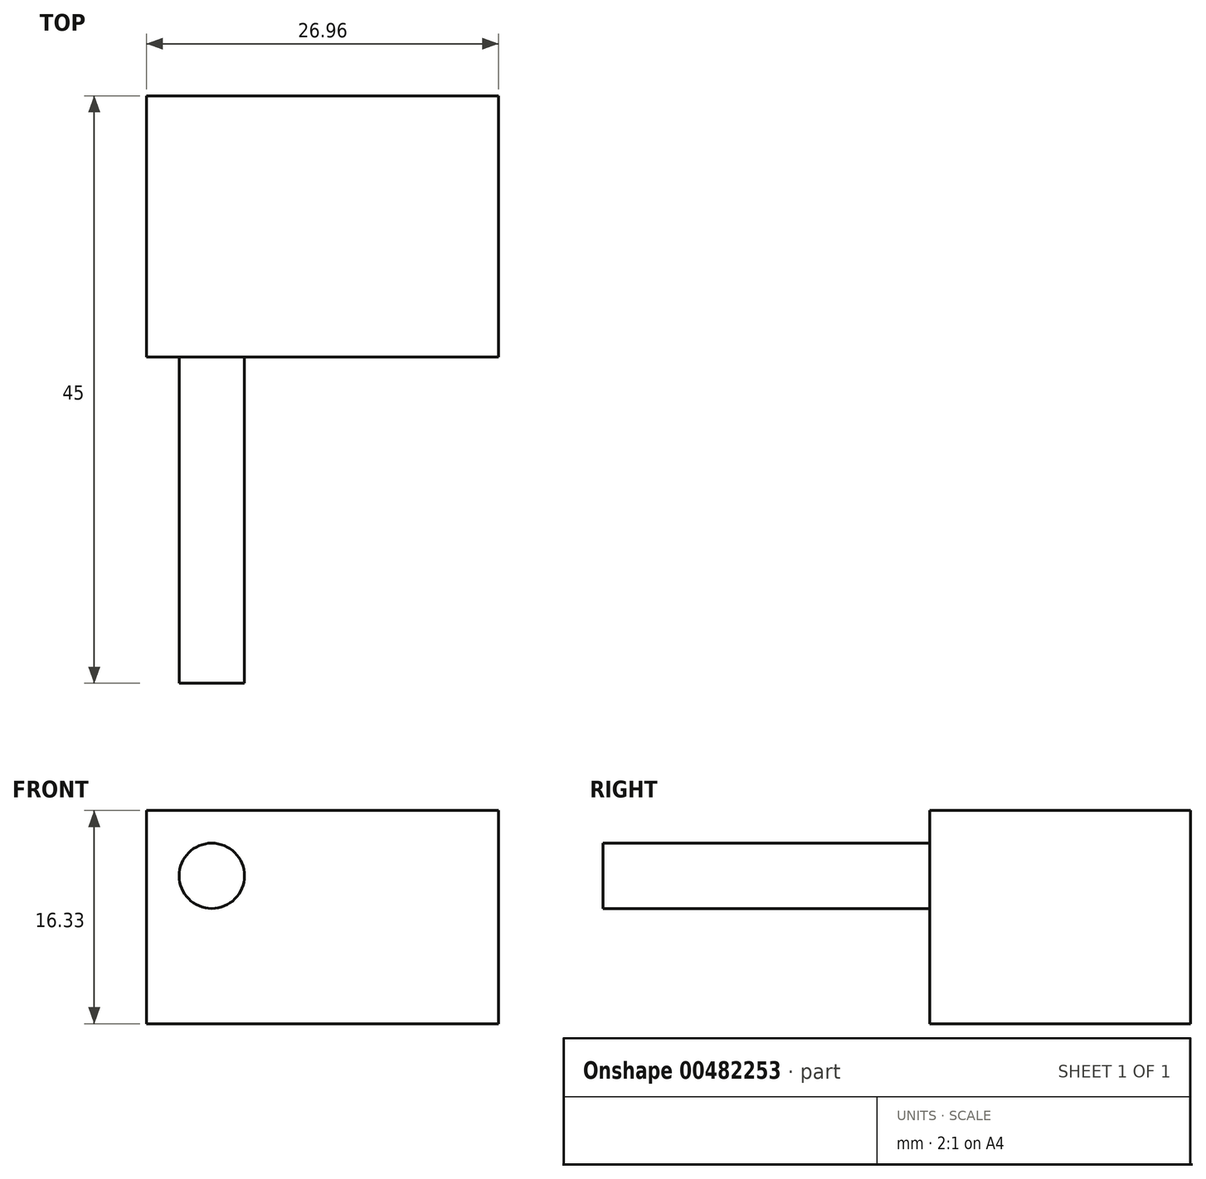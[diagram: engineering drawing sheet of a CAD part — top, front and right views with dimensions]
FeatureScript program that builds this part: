
annotation { "Feature Type Name" : "Feature", "Feature Type Description" : "" }
export const myFeature = defineFeature(function(context is Context, id is Id, definition is map)
    precondition{}
    {
        {
            var Q0;
            Q0=qCreatedBy(makeId("Front.planeOp"),FACE);
            var sketch = newSketch(context, id + "F0", { "sketchPlane" : qUnion([Q0])});
            skLineSegment(sketch, "E0.bottom", {"start": v(-68.77, 60.6) * mm, "end": v(-41.8, 60.6) * mm});
            skLineSegment(sketch, "E0.top", {"start": v(-68.77, 44.28) * mm, "end": v(-41.8, 44.28) * mm});
            skLineSegment(sketch, "E0.left", {"start": v(-68.77, 60.6) * mm, "end": v(-68.77, 44.28) * mm});
            skLineSegment(sketch, "E0.right", {"start": v(-41.8, 60.6) * mm, "end": v(-41.8, 44.28) * mm});
            skSolve(sketch);
        }
        {
            var Q0;
            Q0=makeQuery(id+"F0.imprint","IMPRINT",FACE,{"disambiguationData":[TD([[makeQuery(id+"F0.imprint","IMPRINT",EDGE,{"derivedFrom":sQuery(id+"F0.wireOp",EDGE,"E0.bottom")}),-1.0]])]});
            extrude(context, id + "F1", {"entities" : qUnion([Q0]), "depth" : 20 * mm});
        }
        {
            var Q0;
            Q0=makeQuery(id+"F1.opExtrude","CAP_FACE",FACE,{"disambiguationData":[OSD([sQuery(id+"F0.wireOp",EDGE,"E0.bottom"),sQuery(id+"F0.wireOp",EDGE,"E0.top"),sQuery(id+"F0.wireOp",EDGE,"E0.left"),sQuery(id+"F0.wireOp",EDGE,"E0.right")])],"isStart":false});
            var sketch = newSketch(context, id + "F2", { "sketchPlane" : qUnion([Q0])});
            skCircle(sketch, "E1", {"center": v(-63.77, 55.6) * mm, "radius": 2.5 * mm});
            skSolve(sketch);
        }
        {
            var Q0;
            Q0 = qSketchRegion(id + "F2", true);
            extrude(context, id + "F3", {"entities" : qUnion([Q0]), "depth" : 25 * mm});
        }
        {
            var Q0;
            Q0=makeQuery(id+"F3.opExtrude","CAP_FACE",FACE,{"disambiguationData":[OSD([sQuery(id+"F2.wireOp",EDGE,"E1")])],"isStart":false});
            var sketch = newSketch(context, id + "F4", { "sketchPlane" : qUnion([Q0])});
            skCircle(sketch, "E2", {"center": v(-63.77, 55.6) * mm, "radius": 5.51 * mm});
            skSolve(sketch);
        }
        {
            var Q0;
            Q0=sQuery(id+"F4.wireOp",EDGE,"E2");
            extrude(context, id + "F5", {"bodyType" : ToolBodyType.SURFACE, "surfaceEntities" : qUnion([Q0]), "depth" : 25 * mm});
        }
        {
            var Q0;
            Q0=makeQuery(id+"F5.opExtrude","SWEPT_BODY",BODY,{"disambiguationData":[OSD([sQuery(id+"F4.wireOp",EDGE,"E2")])]});
            deleteBodies(context, id + "F6", {"entities" : qUnion([Q0])});
        }
    });
